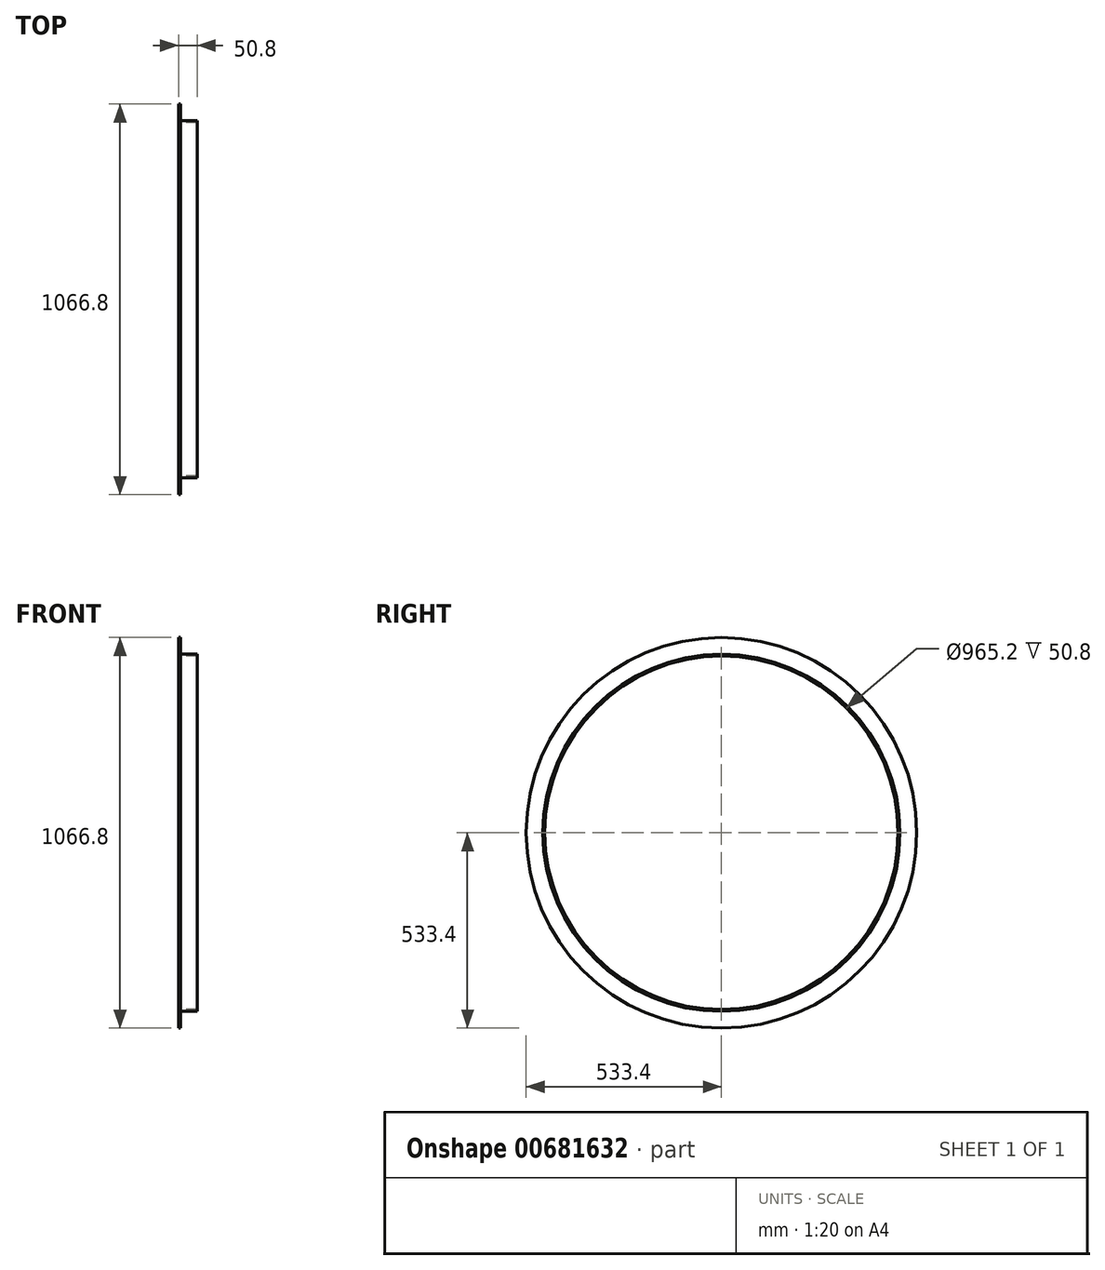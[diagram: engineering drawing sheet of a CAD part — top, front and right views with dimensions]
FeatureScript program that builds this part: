
annotation { "Feature Type Name" : "Feature", "Feature Type Description" : "" }
export const myFeature = defineFeature(function(context is Context, id is Id, definition is map)
    precondition{}
    {
        {
            var Q0;
            Q0=qCreatedBy(makeId("Front.planeOp"),FACE);
            var sketch = newSketch(context, id + "F0", { "sketchPlane" : qUnion([Q0])});
            skLineSegment(sketch, "E0", {"start": v(0, 0) * mm, "end": v(0, 50.8) * mm});
            skLineSegment(sketch, "E1", {"start": v(0, 50.8) * mm, "end": v(5.08, 50.8) * mm});
            skLineSegment(sketch, "E2", {"start": v(5.08, 50.8) * mm, "end": v(5.08, 5.08) * mm});
            skLineSegment(sketch, "E3", {"start": v(5.08, 5.08) * mm, "end": v(50.8, 5.08) * mm});
            skLineSegment(sketch, "E4", {"start": v(50.8, 5.08) * mm, "end": v(50.8, 0) * mm});
            skLineSegment(sketch, "E5", {"start": v(50.8, 0) * mm, "end": v(0, 0) * mm});
            skLineSegment(sketch, "E6", {"start": v(0, 0) * mm, "end": v(0, -482.6) * mm, "construction": true});
            skLineSegment(sketch, "E7", {"start": v(0, -482.6) * mm, "end": v(243.47, -482.6) * mm, "construction": true});
            skSolve(sketch);
        }
        {
            var Q0;
            Q0=makeQuery(id+"F0.imprint","IMPRINT",FACE,{"disambiguationData":[TD([[makeQuery(id+"F0.imprint","IMPRINT",EDGE,{"derivedFrom":sQuery(id+"F0.wireOp",EDGE,"E0")}),-1.0]])]});
            var Q1;
            Q1=sQuery(id+"F0.wireOp",EDGE,"E7");
            revolve(context, id + "F1", {"surfaceOperationType" : NewSurfaceOperationType.NEW, "entities" : qUnion([Q0]), "axis" : qUnion([Q1]), "revolveType" : RevolveType.FULL});
        }
    });
